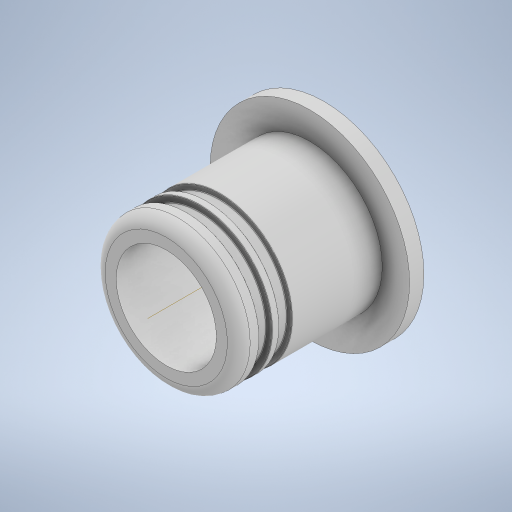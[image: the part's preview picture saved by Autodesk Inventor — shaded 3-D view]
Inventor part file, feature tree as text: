
AUTODESK INVENTOR PART (.ipt)
format: ipt  version: 2024 (Build 280153000, 153)  size: 374,272 bytes
history: native  units: in
note: dims shown in document units (in); Inventor stores cm internally (conversion verified against a paired STEP export)
features: sketch x7, extrude x5, fillet x5, revolve x2, thread x1, other x1
ambient origin geometry x8: Origin, YZ Plane, XZ Plane, XY Plane, X Axis, Y Axis, Z Axis, Center Point
bodies: Solid1 (feature_tree)
feature tree (21):
  extrude  "Extrusion1"  Depth=0.1575in TaperAngle=0.0deg
  extrude  "Extrusion2"  Depth=1.5748in TaperAngle=0.0deg
  extrude  "Extrusion5"  Depth=0.1575in TaperAngle=0.0deg
  thread  "Thread1"  [1 undecoded]
  other  "Work Axis1"
  revolve  "Revolution1"  [1 undecoded]
  fillet  "Fillet1"  [1 undecoded]
  fillet  "Fillet2"  Radius=0.005in
  revolve  "Revolution2"  [1 undecoded]
  fillet  "Fillet3"  Radius=0.07in
  fillet  "Fillet4"  Radius=0.07in
  extrude  "Extrusion7"  Depth=0.065in
  fillet  "Fillet5"  [1 undecoded]
  extrude  "Extrusion8"  Depth=0.005in
  sketch  "Sketch1"  dims[d0=2.19in d1=0.1575in d2=0.0in]
  sketch  "Sketch2"  dims[d3=1.591in d4=1.5748in d5=0.1969in d6=0.0in d7=0.0in]
  sketch  "Sketch5"  dims[d14=0.276in d15=0.64in d16=0.0in d17=0.1575in d18=0.0in]
  sketch  "Sketch7"  dims[d28=0.065in d29=0.007in d30=360.0deg d31=0.005in]
  sketch  "Sketch8"  dims[d32=0.005in d33=0.2953in d34=0.07in d35=0.07in]
  sketch  "Sketch9"  dims[d36=0.065in d37=0.065in d38=90.0deg]
  sketch  "Sketch10"  dims[d39=0.007in d40=0.005in d41=0.64in d42=0.3937in d43=0.0in d46=0.125in d47=1.1in d48=1.5748in d49=0.0in d19=0.0344in d20=0.0344in d50=0.0344in]
note: 5 required parameter values undecoded (feature->parameter linkage not recoverable at this tier; creation-order binding heuristic only, values carry confidence <= 0.55)